# Revit family: rba-bim-rba5502 Series
name_source: partatom
category: Plumbing Fixtures
revit_build: Autodesk Revit 2018 (Build: 20170223_1515(x64)
units: mm (PartAtom-declared; Revit-internal decimal feet)

## family parameters
Always vertical = Yes
Cut with Voids When Loaded = No
Part Type = Normal
Room Calculation Point = No
Round Connector Dimension = Use Diameter
Shared = Yes
Work Plane-Based = No

## types (7) — shared parameters
CW Connection = Yes
HW Connection = Yes
Logo Distance = 50 mm  [stored 0.164042 ft]
Manufacturer = RBA Group
Vent Connection = Yes
Waste Connection = Yes
zero-valued in all types: No. of Outlets

## per-type parameters (varying)
| type | 120 | 160 | 200 | 240 | Depth | Description | L1 | L2 | L3 | L4 | L5 | Length | Materials and Finishes | Middle Bracket | Modified Issue | URL |
| RBA5502-120 | Yes | No | No | No | 140 mm  [stored 0.459318 ft] | 1200mm Wash Trough | 280 mm  [stored 0.918635 ft] | 280 mm  [stored 0.918635 ft] | 280 mm  [stored 0.918635 ft] | 280 mm  [stored 0.918635 ft] | 0 mm  [stored 0 ft] | 1200 mm | Stainless Steel AISI 304, 1.2mm | No | 20210728.01 | www.rba.com.au |
| RBA5502-150 | No | No | No | Yes | 131 mm  [stored 0.42979 ft] | 1500mm Wash Trough | 380 mm | 380 mm | 380 mm | 380 mm | 40 mm  [stored 0.131234 ft] | 1500 mm  [stored 4.92126 ft] | <By Category> | Yes | 20210504.01 |  |
| RBA5502-180 | No | No | No | Yes | 131 mm  [stored 0.42979 ft] | 1800mm Wash Trough | 380 mm | 380 mm | 380 mm | 380 mm | 40 mm  [stored 0.131234 ft] | 1800 mm  [stored 5.90551 ft] | <By Category> | Yes | 20210504.01 |  |
| RBA5502-240 | No | No | No | Yes | 131 mm  [stored 0.42979 ft] | 2400mm Wash Trough | 280 mm  [stored 0.918635 ft] | 280 mm  [stored 0.918635 ft] | 280 mm  [stored 0.918635 ft] | 280 mm  [stored 0.918635 ft] | 0 mm  [stored 0 ft] | 2400 mm | Stainless Steel AISI 304, 1.2mm | Yes | 20210504.01 | www.rba.com.au |
| RBA5502-300 | No | No | No | Yes | 131 mm  [stored 0.42979 ft] | 3000mm Wash Trough | 380 mm | 380 mm | 380 mm | 380 mm | 40 mm  [stored 0.131234 ft] | 3000 mm  [stored 9.84252 ft] | <By Category> | Yes | 20210504.01 |  |
| RBA5502-160 | No | Yes | No | No | 138 mm  [stored 0.452756 ft] | 1600mm Wash Trough | 260 mm  [stored 0.853018 ft] | 260 mm  [stored 0.853018 ft] | 260 mm  [stored 0.853018 ft] | 260 mm  [stored 0.853018 ft] | 0 mm  [stored 0 ft] | 1600 mm  [stored 5.24934 ft] | Stainless Steel AISI 304, 1.2mm | Yes | 20210504.01 | www.rba.com.au |
| RBA5502-200 | No | No | Yes | No | 134 mm  [stored 0.439633 ft] | 2000mm Wash Trough | 260 mm  [stored 0.853018 ft] | 260 mm  [stored 0.853018 ft] | 260 mm  [stored 0.853018 ft] | 260 mm  [stored 0.853018 ft] | 130 mm  [stored 0.426509 ft] | 2000 mm  [stored 6.56168 ft] | Stainless Steel AISI 304, 1.2mm | Yes | 20210504.01 | www.rba.com.au |

note: column(s) folded — value = type name in every type: Model

note: [stored X ft] marks values corroborated as IEEE doubles in the binary element streams (Revit-internal decimal feet)

## geometry (parser evidence)
native form markers: Blend x2, Sweep x2
no freeform markers — native parametric forms only
